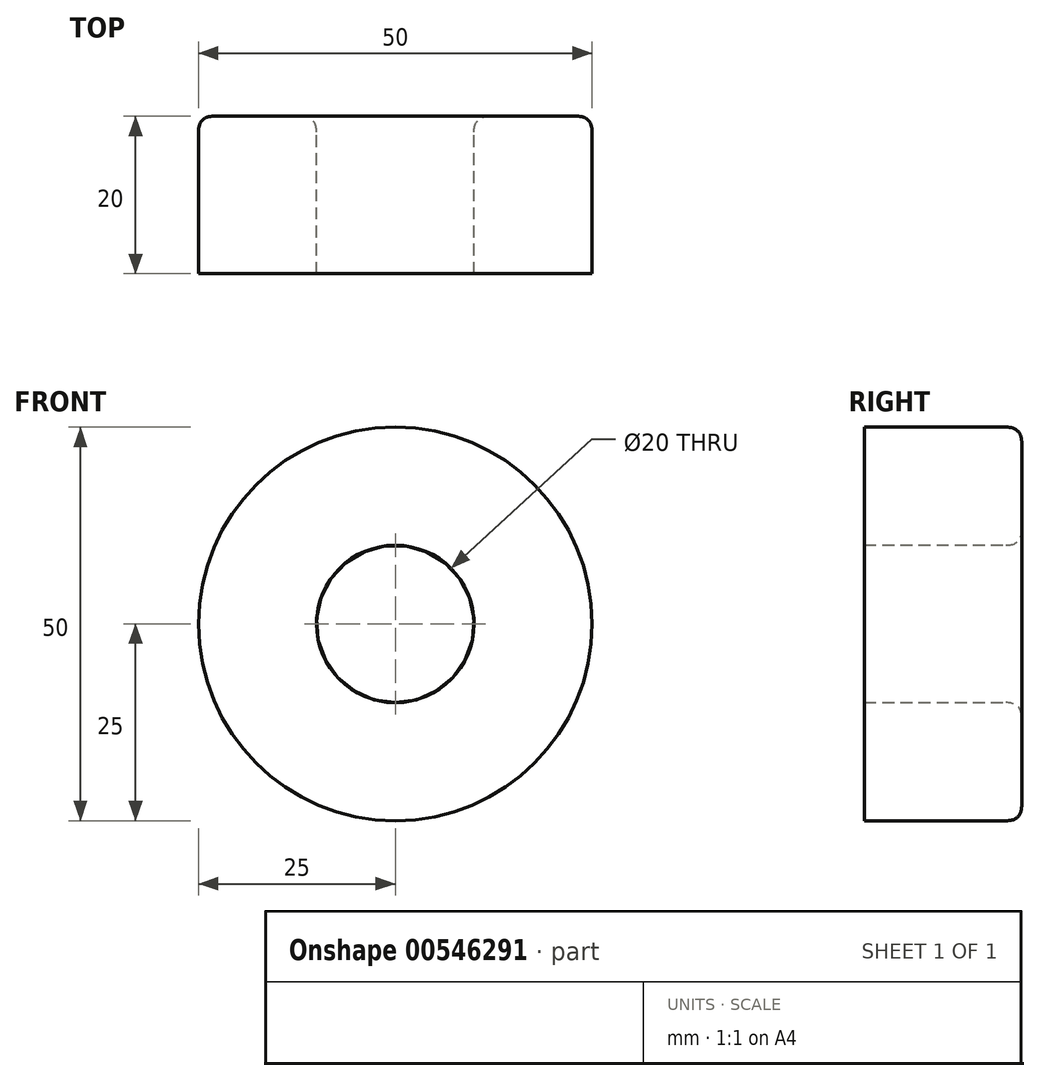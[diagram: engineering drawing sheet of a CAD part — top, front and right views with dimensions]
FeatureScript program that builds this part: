
annotation { "Feature Type Name" : "Feature", "Feature Type Description" : "" }
export const myFeature = defineFeature(function(context is Context, id is Id, definition is map)
    precondition{}
    {
        {
            var Q0;
            Q0=qCreatedBy(makeId("Front.planeOp"),FACE);
            var sketch = newSketch(context, id + "F0", { "sketchPlane" : qUnion([Q0])});
            skCircle(sketch, "E0", {"center": v(0, 0) * mm, "radius": 25 * mm});
            skCircle(sketch, "E1", {"center": v(0, 0) * mm, "radius": 10 * mm});
            skSolve(sketch);
        }
        {
            var Q0;
            Q0 = qSketchRegion(id + "F0", true);
            extrude(context, id + "F1", {"entities" : qUnion([Q0]), "depth" : 20 * mm, "offsetDistance" : 25 * mm});
        }
        {
            var Q0;
            Q0=makeQuery(id+"F1.opExtrude","CAP_FACE",FACE,{"disambiguationData":[OSD([sQuery(id+"F0.wireOp",EDGE,"E0"),sQuery(id+"F0.wireOp",EDGE,"E1")])],"isStart":true});
            fillet(context, id + "F2", {"entities" : qUnion([Q0]), "radius" : 2 * mm, "tangentPropagation" : true, "rho" : 0.5, "crossSection" : FilletCrossSection.CONIC, "allowEdgeOverflow" : false});
        }
    });
